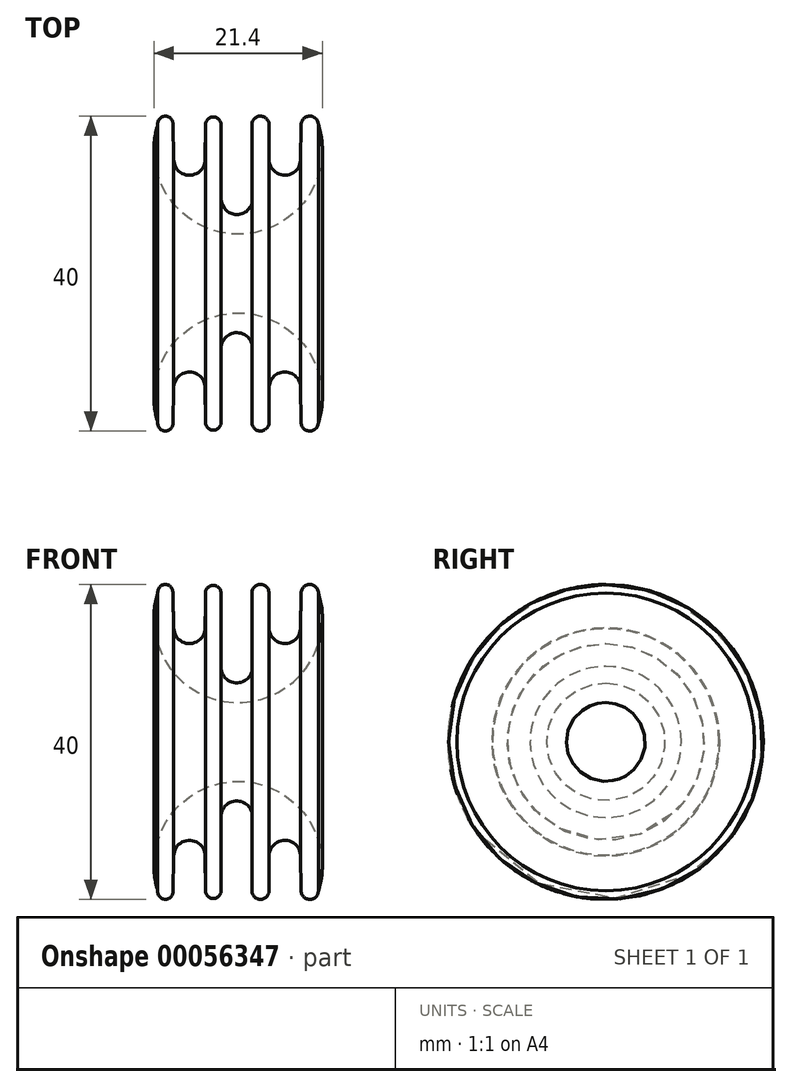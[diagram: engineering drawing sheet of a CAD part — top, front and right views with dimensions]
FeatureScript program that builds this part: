
annotation { "Feature Type Name" : "Feature", "Feature Type Description" : "" }
export const myFeature = defineFeature(function(context is Context, id is Id, definition is map)
    precondition{}
    {
        {
            var Q0;
            Q0=qCreatedBy(makeId("Top.planeOp"),FACE);
            var sketch = newSketch(context, id + "F0", { "sketchPlane" : qUnion([Q0])});
            skLineSegment(sketch, "E0", {"start": v(-8.12, 0.14) * mm, "end": v(-8.02, -4.43) * mm});
            skLineSegment(sketch, "E1", {"start": v(-3.98, 0) * mm, "end": v(-4.02, -4.43) * mm});
            skLineSegment(sketch, "E2", {"start": v(-2, 0) * mm, "end": v(-2, -9.41) * mm});
            skLineSegment(sketch, "E3", {"start": v(1.92, 0) * mm, "end": v(2, -9.3) * mm});
            skLineSegment(sketch, "E4", {"start": v(4.1, 0) * mm, "end": v(4.1, -4.41) * mm});
            skArc(sketch, "E5", {"start": v(-8.12, 0.14) * mm, "mid": v(-9.15, 1.09) * mm, "end": v(-10.04, 0) * mm});
            skArc(sketch, "E6", {"start": v(-8.02, -4.43) * mm, "mid": v(-6.02, -6.41) * mm, "end": v(-4.02, -4.43) * mm});
            skLineSegment(sketch, "E7", {"start": v(8.16, 0) * mm, "end": v(8.1, -4.54) * mm});
            skArc(sketch, "E8", {"start": v(-2, 0) * mm, "mid": v(-2.99, 0.99) * mm, "end": v(-3.98, 0) * mm});
            skArc(sketch, "E9", {"start": v(-2, -9.41) * mm, "mid": v(0.05, -11.41) * mm, "end": v(2, -9.3) * mm});
            skArc(sketch, "E10", {"start": v(4.1, 0) * mm, "mid": v(3, 1.09) * mm, "end": v(1.92, 0) * mm});
            skArc(sketch, "E11", {"start": v(4.1, -4.41) * mm, "mid": v(6.03, -6.41) * mm, "end": v(8.1, -4.54) * mm});
            skArc(sketch, "E12", {"start": v(10.37, 0) * mm, "mid": v(9.27, 1.09) * mm, "end": v(8.16, 0) * mm});
            skArc(sketch, "E13", {"start": v(-10.04, 0) * mm, "mid": v(0.17, -13.91) * mm, "end": v(10.37, 0) * mm});
            skPoint(sketch, "E14", {"position": v(0.17, -13.91) * mm});
            skPoint(sketch, "E15", {"position": v(-9.08, 1.09) * mm});
            skPoint(sketch, "E16", {"position": v(-6.02, -6.41) * mm});
            skPoint(sketch, "E17", {"position": v(0, -11.41) * mm});
            skPoint(sketch, "E18", {"position": v(6.16, -6.41) * mm});
            skPoint(sketch, "E18.positionSnap0", {"position": v(6.03, -6.41) * mm});
            skPoint(sketch, "E19", {"position": v(-2.99, 1.09) * mm});
            skPoint(sketch, "E19.positionSnap0", {"position": v(9.27, 1.09) * mm});
            skPoint(sketch, "E20", {"position": v(3, 1.09) * mm});
            skLineSegment(sketch, "E21", {"start": v(-13.15, -18.91) * mm, "end": v(17.21, -18.91) * mm, "construction": true});
            skSolve(sketch);
        }
        {
            var Q0;
            Q0=makeQuery(id+"F0.imprint","IMPRINT",FACE,{"disambiguationData":[TD([[makeQuery(id+"F0.imprint","IMPRINT",EDGE,{"derivedFrom":sQuery(id+"F0.wireOp",EDGE,"E0")}),-1.0]])]});
            var Q1;
            Q1=sQuery(id+"F0.wireOp",EDGE,"E21");
            revolve(context, id + "F1", {"entities" : qUnion([Q0]), "axis" : qUnion([Q1]), "revolveType" : RevolveType.FULL});
        }
    });
